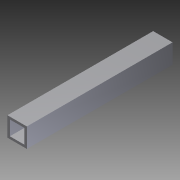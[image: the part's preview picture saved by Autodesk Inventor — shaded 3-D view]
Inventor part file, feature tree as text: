
AUTODESK INVENTOR PART (.ipt)
format: ipt  version: 2012 (Build 160160000, 160)  size: 76,800 bytes
history: native  units: in
note: dims shown in document units (in); Inventor stores cm internally (conversion verified against a paired STEP export)
features: extrude x1, sketch x1
ambient origin geometry x8: Origin, YZ Plane, XZ Plane, XY Plane, X Axis, Y Axis, Z Axis, Center Point
bodies: Solid1 (feature_tree)
feature tree (2):
  extrude  "Extrusion1"  Depth=0.125in
  sketch  "Sketch1"  dims[d0=0.125in d1=0.125in d2=0.125in d3=0.125in d4=1.0in d5=1.0in d6=7.5in d7=0.0in]
